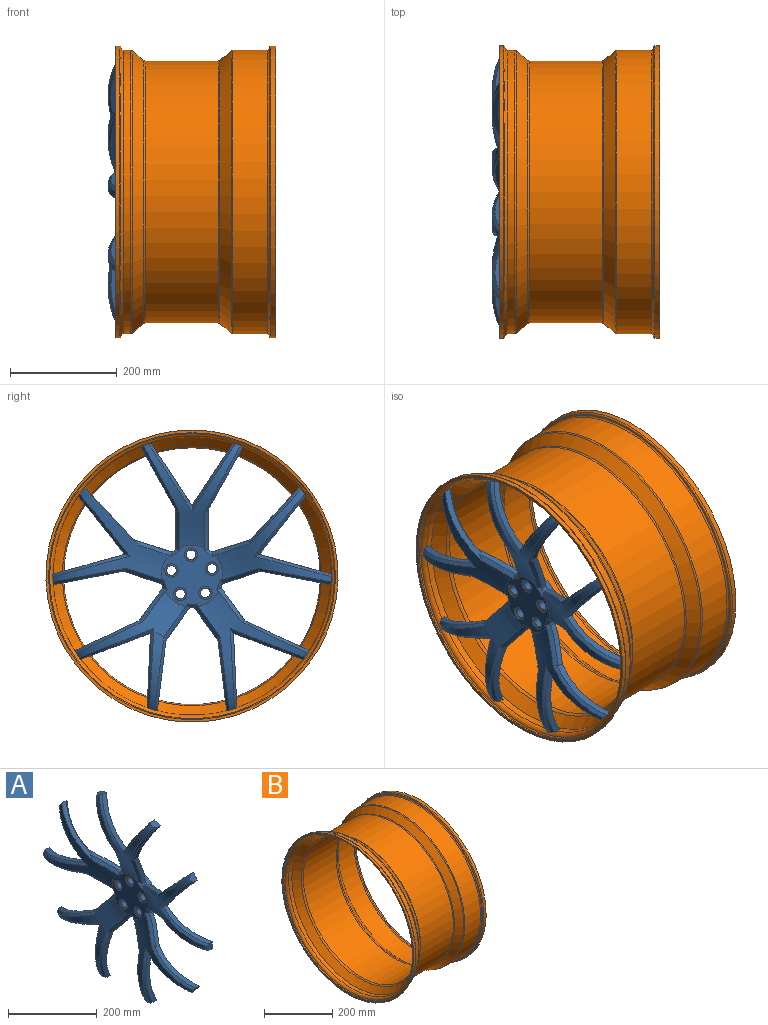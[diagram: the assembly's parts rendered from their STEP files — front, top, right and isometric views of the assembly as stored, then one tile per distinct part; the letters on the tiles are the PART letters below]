
ASSEMBLY  parts=2 mates=1
PART A: 112 faces, bbox 65.9x536.3x523.3 mm
  f0: cylinder r=260.33mm len=17mm, axis (1,0,0), area 304.7mm2, adj f9,f14,f43,f51,f72,f74
  f1: cylinder r=260.33mm len=19.78mm, axis (1,0,0), area 304.7mm2, adj f10,f15,f46,f50,f75,f77
  f2: cylinder r=260.33mm len=18.96mm, axis (1,0,0), area 304.7mm2, adj f9,f14,f41,f44,f71,f73
  f3: cylinder r=260.33mm len=18.96mm, axis (1,0,0), area 304.7mm2, adj f11,f16,f25,f42,f68,f70
  f4: cylinder r=260.33mm len=18.66mm, axis (1,0,0), area 304.7mm2, adj f12,f17,f27,f36,f80,f82
  f5: cylinder r=260.33mm len=19.78mm, axis (1,0,0), area 304.7mm2, adj f13,f18,f29,f34,f83,f86
  f6: cylinder r=260.33mm len=17mm, axis (1,0,0), area 311.8mm2, adj f13,f18,f30,f35,f84,f85
  f7: cylinder r=260.33mm len=18.66mm, axis (1,0,0), area 304.7mm2, adj f12,f17,f21,f28,f79,f81
  f8: cylinder r=260.33mm len=17mm, axis (1,0,0), area 304.7mm2, adj f11,f16,f26,f33,f67,f69
  f9: revolved ~226.97x215.68mm, area 8260.5mm2, adj f0,f2,f20,f71,f72,f73,f74,f89
  f10: revolved ~217.82x206.87mm, area 8260.5mm2, adj f1,f19,f20,f75,f76,f77,f78,f91
  f11: revolved ~226.97x215.68mm, area 8259.9mm2, adj f3,f8,f20,f67,f68,f69,f70,f87
  f12: revolved ~217.51x207.79mm, area 8266.7mm2, adj f4,f7,f20,f79,f80,f81,f82,f93
  f13: revolved ~217.82x206.87mm, area 8959.7mm2, adj f5,f6,f20,f35,f83,f85,f86,f95
  f14: revolved ~245.74x241.71mm, area 11883.8mm2, adj f0,f2,f40,f41,f43,f44,f47,f48
  f15: revolved ~278.65x223.71mm, area 11880.8mm2, adj f1,f19,f22,f23,f45,f46,f47,f49
  f16: revolved ~245.74x241.71mm, area 11883.8mm2, adj f3,f8,f25,f26,f32,f33,f39,f42
  f17: revolved ~300.43x213.1mm, area 11883.8mm2, adj f4,f7,f21,f24,f27,f28,f36,f37
  f18: revolved ~285.72x225.72mm, area 11312mm2, adj f5,f6,f29,f30,f31,f34,f38,f47
  f19: cylinder r=260.33mm len=17mm, axis (1,0,0), area 304.7mm2, adj f10,f15,f22,f45,f76,f78
  f20: plane 115.68x114.55mm, normal (-1,0,0), area 7532.8mm2, adj f9,f10,f11,f12,f13,f52,f54,f56
  f21: plane 121.5x67.64mm, normal (0,-0.87,-0.48), area 1609.9mm2, adj f7,f17,f24,f79,f93
  f22: plane 101.56x94.87mm, normal (0,0.73,0.68), area 1609.4mm2, adj f15,f19,f23,f78,f92
  f23: plane 75.95x37.13mm, normal (0,0.31,0.95), area 857.6mm2, adj f15,f22,f47,f92
  f24: plane 77.46x36.83mm, normal (0,-1,0), area 847.6mm2, adj f17,f21,f93,f100
  f25: plane 140.06x32.47mm, normal (0,1,0.04), area 1693.2mm2, adj f3,f16,f26,f68
  f26: plane 131.35x49.53mm, normal (0,-0.35,-0.94), area 1693.3mm2, adj f8,f16,f25,f69
  f27: plane 117.03x77.64mm, normal (0,-0.83,0.55), area 1693.2mm2, adj f4,f17,f28,f80
  f28: plane 117.03x77.63mm, normal (0,0.83,0.55), area 1693.3mm2, adj f7,f17,f27,f81
  f29: plane 135.13x37.9mm, normal (0,0.27,0.96), area 1693.2mm2, adj f5,f18,f30,f86
  f30: plane 110.33x88.03mm, normal (0,0.78,-0.62), area 1689.5mm2, adj f6,f18,f29,f85
  f31: plane 73.82x36.83mm, normal (0,0.31,-0.95), area 847.6mm2, adj f18,f34,f95,f98
  f32: plane 63.25x46.78mm, normal (0,0.81,0.59), area 847.6mm2, adj f16,f33,f87,f105
  f33: plane 125.8x59.21mm, normal (0,0.42,0.91), area 1609.9mm2, adj f8,f16,f32,f67,f87
  f34: plane 136.15x32.79mm, normal (0,-0.19,-0.98), area 1609.3mm2, adj f5,f18,f31,f83,f95
  f35: plane 109.35x102.19mm, normal (0,-0.73,0.68), area 1668.9mm2, adj f6,f13,f38,f84,f96
  f36: plane 121.5x67.63mm, normal (0,0.87,-0.48), area 1609.9mm2, adj f4,f17,f37,f82,f94
  f37: plane 77.46x36.83mm, normal (0,1,0), area 847.6mm2, adj f17,f36,f94,f99
  f38: plane 84.5x36.73mm, normal (0,-0.31,0.95), area 882.9mm2, adj f18,f35,f84,f96,f97
  f39: plane 63.24x46.77mm, normal (0,-0.81,-0.59), area 847.6mm2, adj f16,f42,f88,f104
  f40: plane 63.25x46.78mm, normal (0,0.81,-0.59), area 847.6mm2, adj f14,f41,f89,f103
  f41: plane 137.71x32.89mm, normal (0,0.99,-0.12), area 1609.9mm2, adj f2,f14,f40,f71,f89
  f42: plane 137.63x32.79mm, normal (0,-0.99,-0.12), area 1609.4mm2, adj f3,f16,f39,f70,f88
  f43: plane 131.35x49.53mm, normal (0,0.35,-0.94), area 1693.2mm2, adj f0,f14,f44,f72
  f44: plane 140.06x32.47mm, normal (0,-1,0.04), area 1693.3mm2, adj f2,f14,f43,f73
  f45: plane 109.84x87.54mm, normal (0,-0.78,-0.62), area 1693.2mm2, adj f15,f19,f46,f76
  f46: plane 135.13x37.89mm, normal (0,-0.27,0.96), area 1693.3mm2, adj f1,f15,f45,f77
  f47: cylinder r=57.83mm len=115.67mm, axis (1,0,0), area 4232.5mm2, adj f14,f15,f16,f17,f18,f23,f87,f88
  f48: plane 63.24x46.77mm, normal (0,-0.81,0.59), area 847.6mm2, adj f14,f51,f90,f102
  f49: plane 73.82x36.83mm, normal (0,-0.31,-0.95), area 847.6mm2, adj f15,f50,f91,f101
  f50: plane 136.23x32.89mm, normal (0,0.19,-0.98), area 1609.9mm2, adj f1,f15,f49,f75,f91
  f51: plane 125.71x59.12mm, normal (0,-0.42,0.91), area 1609.4mm2, adj f0,f14,f48,f74,f90
  f52: cylinder r=12.5mm len=25mm, axis (-1,0,0), area 235.6mm2, adj f20,f53
  f53: plane 25x25mm, normal (-1,0,0), area 236.4mm2, adj f52,f66
  f54: cylinder r=12.5mm len=25mm, axis (-1,0,0), area 235.6mm2, adj f20,f55
  f55: plane 25x25mm, normal (-1,0,0), area 236.4mm2, adj f54,f65
  f56: cylinder r=12.5mm len=25mm, axis (-1,0,0), area 235.6mm2, adj f20,f57
  f57: plane 25x25mm, normal (-1,0,0), area 236.4mm2, adj f56,f64
  f58: cylinder r=12.5mm len=25mm, axis (-1,0,0), area 235.6mm2, adj f20,f59
  f59: plane 25x25mm, normal (-1,0,0), area 236.4mm2, adj f58,f63
  f60: cylinder r=12.5mm len=25mm, axis (-1,0,0), area 235.6mm2, adj f20,f61
  f61: plane 25x25mm, normal (-1,0,0), area 236.4mm2, adj f60,f62
  f62: cylinder r=9mm len=25mm, axis (-1,0,0), area 1413.7mm2, adj f61,f111
  f63: cylinder r=9mm len=25mm, axis (-1,0,0), area 1413.7mm2, adj f59,f111
  f64: cylinder r=9mm len=25mm, axis (-1,0,0), area 1413.7mm2, adj f57,f111
  f65: cylinder r=9mm len=25mm, axis (-1,0,0), area 1413.7mm2, adj f55,f111
  f66: cylinder r=9mm len=25mm, axis (-1,0,0), area 1413.7mm2, adj f53,f111
  f67: bspline ~128.84x64.7mm, area 1029mm2, adj f8,f11,f33,f87
  f68: bspline ~151.52x25.13mm, area 1072.3mm2, adj f3,f11,f25,f69
  f69: bspline ~142.25x57.74mm, area 1072.5mm2, adj f8,f11,f26,f68
  f70: bspline ~146.12x29.28mm, area 1029.2mm2, adj f3,f11,f42,f88
  f71: bspline ~146.06x29.14mm, area 1029mm2, adj f2,f9,f41,f89
  f72: bspline ~142.25x57.74mm, area 1072.3mm2, adj f0,f9,f43,f73
  f73: bspline ~151.52x25.13mm, area 1072.5mm2, adj f2,f9,f44,f72
  f74: bspline ~133.09x66.68mm, area 1029.2mm2, adj f0,f9,f51,f90
  f75: bspline ~144.79x31.87mm, area 1029mm2, adj f1,f10,f50,f91
  f76: bspline ~120.24x97.29mm, area 1072.3mm2, adj f10,f19,f45,f77
  f77: bspline ~146.72x44.21mm, area 1072.5mm2, adj f1,f10,f46,f76
  f78: bspline ~108.5x103.49mm, area 1029.2mm2, adj f10,f19,f22,f92
  f79: bspline ~130.12x73.78mm, area 1029mm2, adj f7,f12,f21,f93
  f80: bspline ~127.55x86.46mm, area 1072.3mm2, adj f4,f12,f27,f81
  f81: bspline ~127.55x86.46mm, area 1072.5mm2, adj f7,f12,f28,f80
  f82: bspline ~130.12x73.78mm, area 1029.4mm2, adj f4,f12,f36,f94
  f83: bspline ~144.82x31.88mm, area 1029.4mm2, adj f5,f13,f34,f95
  f84: bspline ~101.02x93.77mm, area 943.4mm2, adj f6,f18,f35,f38
  f85: bspline ~120.24x97.29mm, area 1072.5mm2, adj f6,f13,f30,f86
  f86: bspline ~146.72x44.21mm, area 1072.3mm2, adj f5,f13,f29,f85
  f87: bspline ~83.02x66.96mm, area 747.9mm2, adj f11,f20,f32,f33,f47,f67,f105,f106
  f88: bspline ~86.7x64.15mm, area 747.9mm2, adj f11,f20,f39,f42,f47,f70,f104,f107
  f89: bspline ~86.71x64.15mm, area 747.9mm2, adj f9,f20,f40,f41,f47,f71,f103,f107
  f90: bspline ~83.02x66.96mm, area 747.9mm2, adj f9,f20,f47,f48,f51,f74,f102,f108
  f91: bspline ~97.96x39.87mm, area 747.9mm2, adj f10,f20,f47,f49,f50,f75,f101,f108
  f92: bspline ~93.46x38.6mm, area 744mm2, adj f10,f20,f22,f23,f47,f78,f109
  f93: bspline ~99.62x39.87mm, area 747.9mm2, adj f12,f20,f21,f24,f47,f79,f100,f109
  f94: bspline ~99.62x39.87mm, area 747.9mm2, adj f12,f20,f36,f37,f47,f82,f99,f110
  f95: bspline ~97.96x39.87mm, area 747.9mm2, adj f13,f20,f31,f34,f47,f83,f98,f106
  f96: bspline ~83.6x37.49mm, area 716.3mm2, adj f13,f20,f35,f38,f47,f97,f110
  f97: cylinder r=5mm len=10.15mm, axis (1,0,0), area 41.4mm2, adj f18,f38,f47,f96
  f98: cylinder r=5mm len=10.15mm, axis (1,0,0), area 41.4mm2, adj f18,f31,f47,f95
  f99: cylinder r=5mm len=10.15mm, axis (1,0,0), area 41.4mm2, adj f17,f37,f47,f94
  f100: cylinder r=5mm len=10.15mm, axis (1,0,0), area 41.4mm2, adj f17,f24,f47,f93
  f101: cylinder r=5mm len=10.15mm, axis (1,0,0), area 41.4mm2, adj f15,f47,f49,f91
  f102: cylinder r=5mm len=10.15mm, axis (1,0,0), area 41.4mm2, adj f14,f47,f48,f90
  f103: cylinder r=5mm len=10.15mm, axis (1,0,0), area 41.4mm2, adj f14,f40,f47,f89
  f104: cylinder r=5mm len=10.15mm, axis (1,0,0), area 41.4mm2, adj f16,f39,f47,f88
  f105: cylinder r=5mm len=10.15mm, axis (1,0,0), area 41.4mm2, adj f16,f32,f47,f87
  f106: cone r=57.83mm half-angle=45deg, axis (1,0,0), area 109.8mm2, adj f20,f47,f87,f95
  f107: cone r=57.83mm half-angle=45deg, axis (1,0,0), area 109.8mm2, adj f20,f47,f88,f89
  f108: cone r=57.83mm half-angle=45deg, axis (1,0,0), area 109.8mm2, adj f20,f47,f90,f91
  f109: cone r=57.83mm half-angle=45deg, axis (1,0,0), area 109.8mm2, adj f20,f47,f92,f93
  f110: cone r=57.83mm half-angle=45deg, axis (1,0,0), area 109.8mm2, adj f20,f47,f94,f96
  f111: plane 115.67x115.67mm, normal (1,0,0), area 9235.2mm2, adj f47,f62,f63,f64,f65,f66
PART B: 32 faces, bbox 300x592x592 mm
  f0: torus R=270.33mm, axis (-1,0,0), area 13183.2mm2, adj f1,f31
  f1: plane 543.19x543.19mm, normal (1,0,0), area 2151.7mm2, adj f0,f2
  f2: torus R=271.59mm, axis (-1,0,0), area 4995.5mm2, adj f1,f3
  f3: cylinder r=273.45mm len=546.9mm, axis (-1,0,0), area 13993.2mm2, adj f2,f4
  f4: plane 546.9x546.9mm, normal (-1,0,0), area 8512.1mm2, adj f3,f5
  f5: cylinder r=268.45mm len=536.9mm, axis (-1,0,0), area 4977.4mm2, adj f4,f6
  f6: torus R=265.45mm, axis (-1,0,0), area 5986.4mm2, adj f5,f7
  f7: torus R=270.33mm, axis (-1,0,0), area 19561.2mm2, adj f6,f8
  f8: cylinder r=260.33mm len=520.66mm, axis (-1,0,0), area 21558.8mm2, adj f7,f9
  f9: cone r=260.33mm half-angle=40deg, axis (-1,0,0), area 43416.2mm2, adj f8,f10
  f10: torus R=250.33mm, axis (-1,0,0), area 10576.8mm2, adj f9,f11
  f11: cylinder r=240.33mm len=480.66mm, axis (-1,0,0), area 205909.2mm2, adj f10,f12
  f12: torus R=250.33mm, axis (-1,0,0), area 10576.8mm2, adj f11,f13
  f13: cone r=242.67mm half-angle=40deg, axis (1,0,0), area 43416.2mm2, adj f12,f14
  f14: cylinder r=260.33mm len=520.66mm, axis (-1,0,0), area 106615.3mm2, adj f13,f15
  f15: torus R=268.33mm, axis (-1,0,0), area 17224.7mm2, adj f14,f16
  f16: torus R=265.45mm, axis (-1,0,0), area 6588.5mm2, adj f15,f17
  f17: cylinder r=268.45mm len=536.9mm, axis (-1,0,0), area 7950.7mm2, adj f16,f18
  f18: plane 546.9x546.9mm, normal (1,0,0), area 8512.1mm2, adj f17,f19
  f19: cylinder r=273.45mm len=546.9mm, axis (-1,0,0), area 16029.9mm2, adj f18,f20
  f20: torus R=270.45mm, axis (-1,0,0), area 8064.2mm2, adj f19,f21
  f21: plane 540.9x540.9mm, normal (-1,0,0), area 3587.4mm2, adj f20,f22
  f22: torus R=268.33mm, axis (-1,0,0), area 7888.4mm2, adj f21,f23
  f23: cylinder r=265.33mm len=530.66mm, axis (-1,0,0), area 108663mm2, adj f22,f24
  f24: torus R=260.33mm, axis (-1,0,0), area 5810.6mm2, adj f23,f25
  f25: cone r=246.5mm half-angle=40deg, axis (1,0,0), area 44077.4mm2, adj f24,f26
  f26: torus R=250.33mm, axis (-1,0,0), area 5389.4mm2, adj f25,f27
  f27: cylinder r=245.33mm len=490.66mm, axis (-1,0,0), area 210193.1mm2, adj f26,f28
  f28: torus R=250.33mm, axis (-1,0,0), area 5389.4mm2, adj f27,f29
  f29: cone r=264.16mm half-angle=40deg, axis (-1,0,0), area 44077.4mm2, adj f28,f30
  f30: torus R=260.33mm, axis (-1,0,0), area 5810.6mm2, adj f29,f31
  f31: cylinder r=265.33mm len=530.66mm, axis (-1,0,0), area 21972.9mm2, adj f0,f30
PLACE A t=(-361.81,29.75,52.28)mm
PLACE B t=(-217.62,-28.08,52.28)mm
MATE cylindrical A.f0 <-> B.f3  axis (1,0,0) through (-318.39,-28.08,52.28)mm
